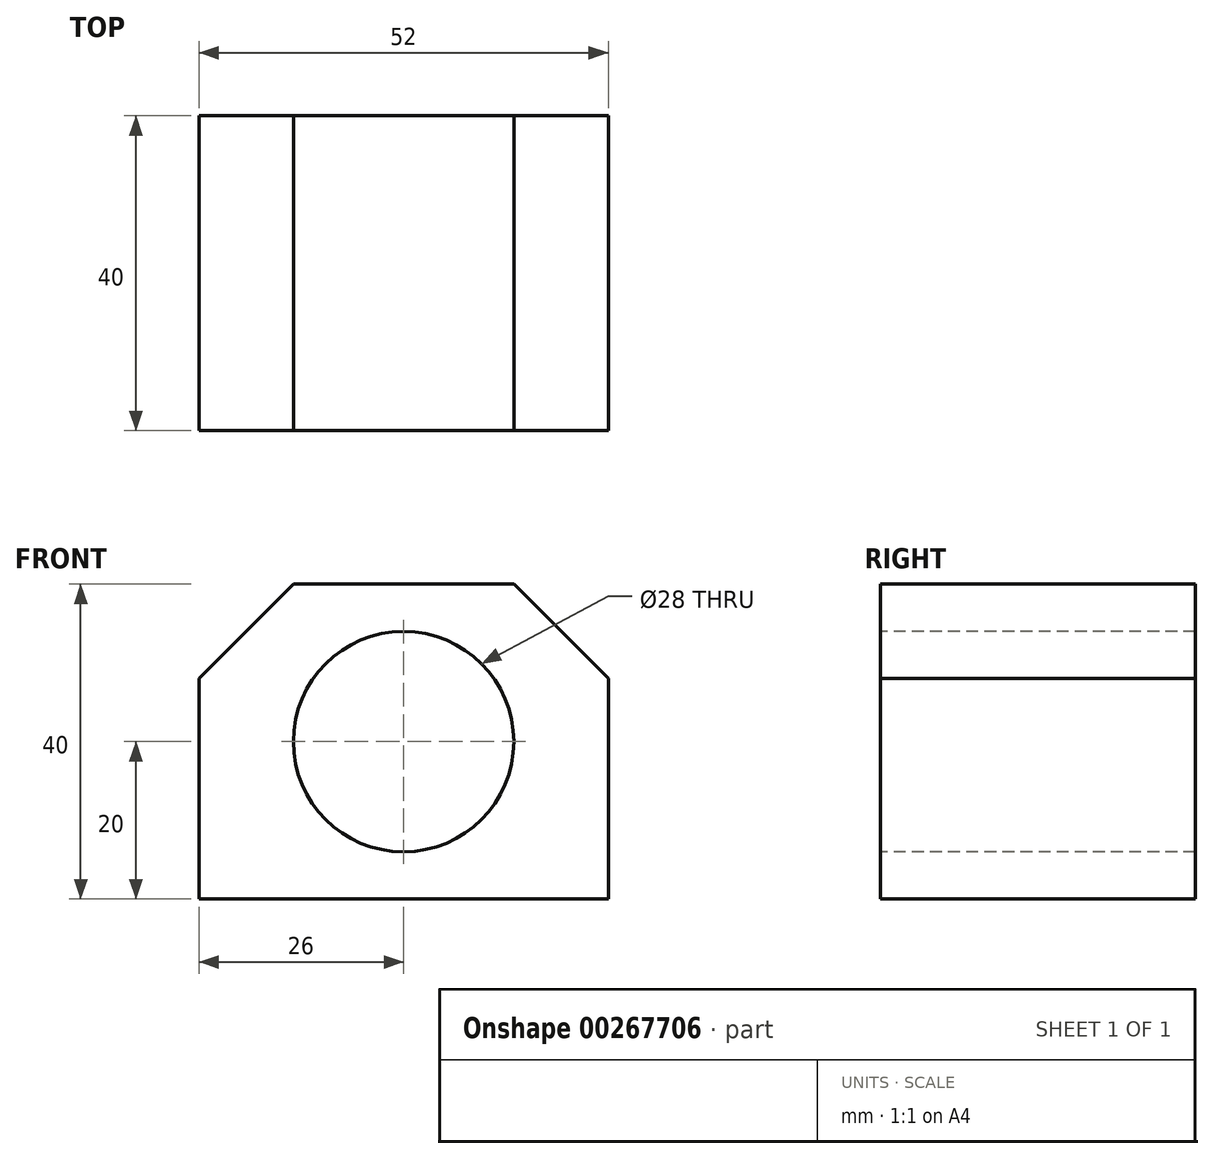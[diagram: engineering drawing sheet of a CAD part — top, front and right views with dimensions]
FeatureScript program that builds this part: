
annotation { "Feature Type Name" : "Feature", "Feature Type Description" : "" }
export const myFeature = defineFeature(function(context is Context, id is Id, definition is map)
    precondition{}
    {
        {
            var Q0;
            Q0=qCreatedBy(makeId("Front.planeOp"),FACE);
            var sketch = newSketch(context, id + "F0", { "sketchPlane" : qUnion([Q0])});
            skLineSegment(sketch, "E0.bottom", {"start": v(-14, 20) * mm, "end": v(14, 20) * mm});
            skLineSegment(sketch, "E0.top", {"start": v(-26, -20) * mm, "end": v(26, -20) * mm});
            skLineSegment(sketch, "E0.left", {"start": v(-26, 8) * mm, "end": v(-26, -20) * mm});
            skLineSegment(sketch, "E0.right", {"start": v(26, 8) * mm, "end": v(26, -20) * mm});
            skPoint(sketch, "E0.middle", {"position": v(0, 0) * mm});
            skLineSegment(sketch, "E1", {"start": v(-26, 8) * mm, "end": v(-14, 20) * mm});
            skLineSegment(sketch, "E2", {"start": v(14, 20) * mm, "end": v(26, 8) * mm});
            skPoint(sketch, "E3.orphan", {"position": v(-26, 20) * mm});
            skPoint(sketch, "E4.orphan", {"position": v(26, 20) * mm});
            skCircle(sketch, "E5", {"center": v(0, 0) * mm, "radius": 14 * mm});
            skSolve(sketch);
        }
        {
            var Q0;
            Q0 = qSketchRegion(id + "F0", true);
            extrude(context, id + "F1", {"entities" : qUnion([Q0]), "oppositeDirection" : true, "depth" : 40 * mm});
        }
    });
